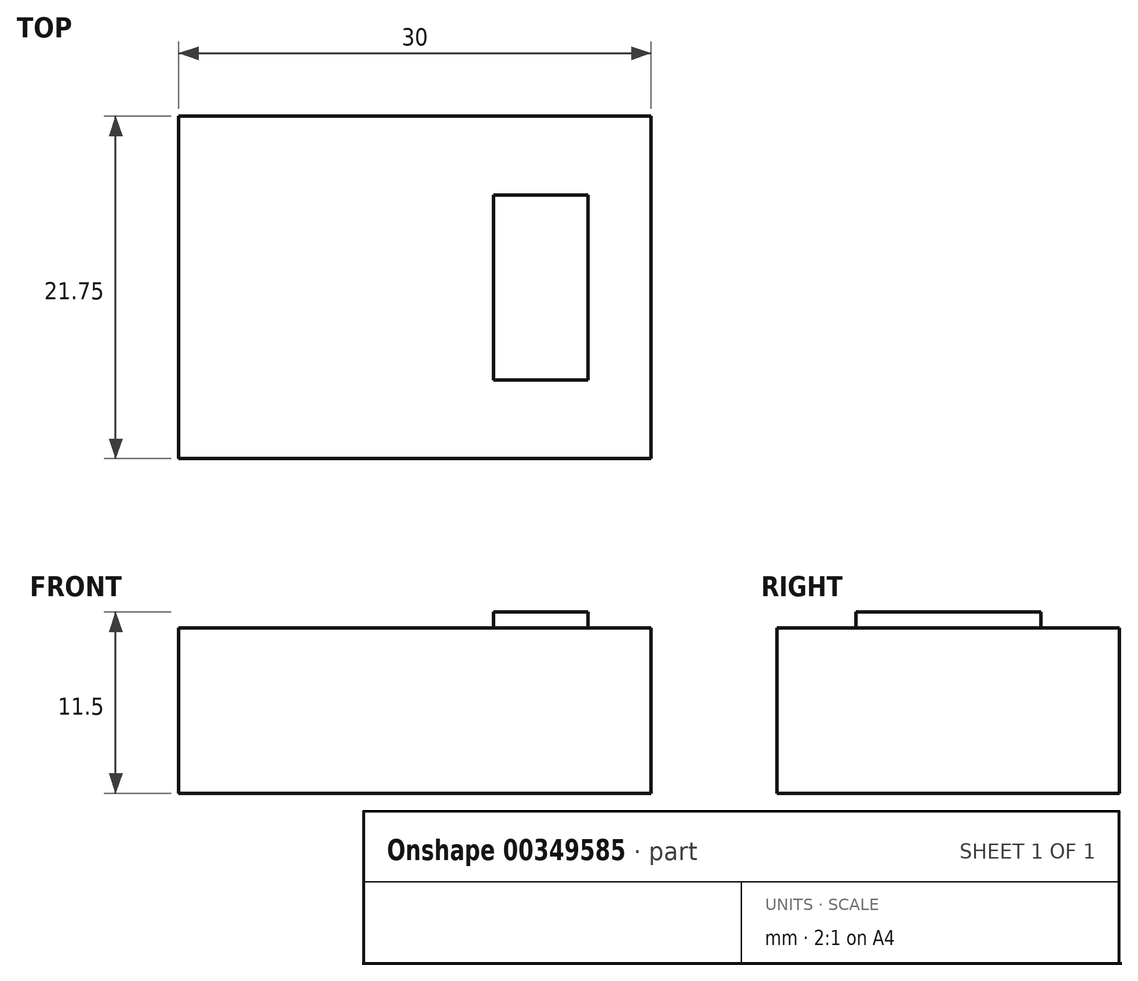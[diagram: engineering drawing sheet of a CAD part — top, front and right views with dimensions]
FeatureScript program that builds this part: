
annotation { "Feature Type Name" : "Feature", "Feature Type Description" : "" }
export const myFeature = defineFeature(function(context is Context, id is Id, definition is map)
    precondition{}
    {
        {
            var Q0;
            Q0=qCreatedBy(makeId("Front.planeOp"),FACE);
            var sketch = newSketch(context, id + "F0", { "sketchPlane" : qUnion([Q0])});
            skLineSegment(sketch, "E0.bottom", {"start": v(-1, 0.35) * mm, "end": v(1, 0.35) * mm});
            skLineSegment(sketch, "E0.top", {"start": v(-1, -0.35) * mm, "end": v(1, -0.35) * mm});
            skLineSegment(sketch, "E0.left", {"start": v(-1, 0.35) * mm, "end": v(-1, -0.35) * mm});
            skLineSegment(sketch, "E0.right", {"start": v(1, 0.35) * mm, "end": v(1, -0.35) * mm});
            skPoint(sketch, "E0.middle", {"position": v(0, 0) * mm});
            skSolve(sketch);
        }
        {
            var Q0;
            Q0=qSketchRegion(id+"F0",true);
            extrude(context, id + "F1", {"entities" : qUnion([Q0]), "depth" : 1.45 * mm});
        }
        {
            var Q0;
            Q0=makeQuery(id+"F1.opExtrude","SWEPT_BODY",BODY,{"disambiguationData":[OSD([sQuery(id+"F0.wireOp",EDGE,"E0.bottom"),sQuery(id+"F0.wireOp",EDGE,"E0.top"),sQuery(id+"F0.wireOp",EDGE,"E0.left"),sQuery(id+"F0.wireOp",EDGE,"E0.right")])]});
            var Q1;
            Q1=qCreatedBy(makeId("Origin.pointOp"),VERTEX);
            transform(context, id + "F2", {"entities" : qUnion([Q0]), "transformType" : TransformType.SCALE_UNIFORMLY, "scale" : 15, "scalePoint" : qUnion([Q1]), "makeCopy" : false});
        }
        {
            var Q0;
            Q0=makeQuery(id+"F1.opExtrude","SWEPT_FACE",FACE,{"disambiguationData":[OSD([sQuery(id+"F0.wireOp",EDGE,"E0.bottom")])]});
            var sketch = newSketch(context, id + "F3", { "sketchPlane" : qUnion([Q0])});
            skLineSegment(sketch, "E1.bottom", {"start": v(5, -5) * mm, "end": v(11, -5) * mm});
            skLineSegment(sketch, "E1.top", {"start": v(5, -16.75) * mm, "end": v(11, -16.75) * mm});
            skLineSegment(sketch, "E1.left", {"start": v(5, -5) * mm, "end": v(5, -16.75) * mm});
            skLineSegment(sketch, "E1.right", {"start": v(11, -5) * mm, "end": v(11, -16.75) * mm});
            skSolve(sketch);
        }
        {
            var Q0;
            Q0 = qSketchRegion(id + "F3", true);
            extrude(context, id + "F4", {"entities" : qUnion([Q0]), "operationType" : NewBodyOperationType.ADD, "depth" : 1 * mm});
        }
    });
